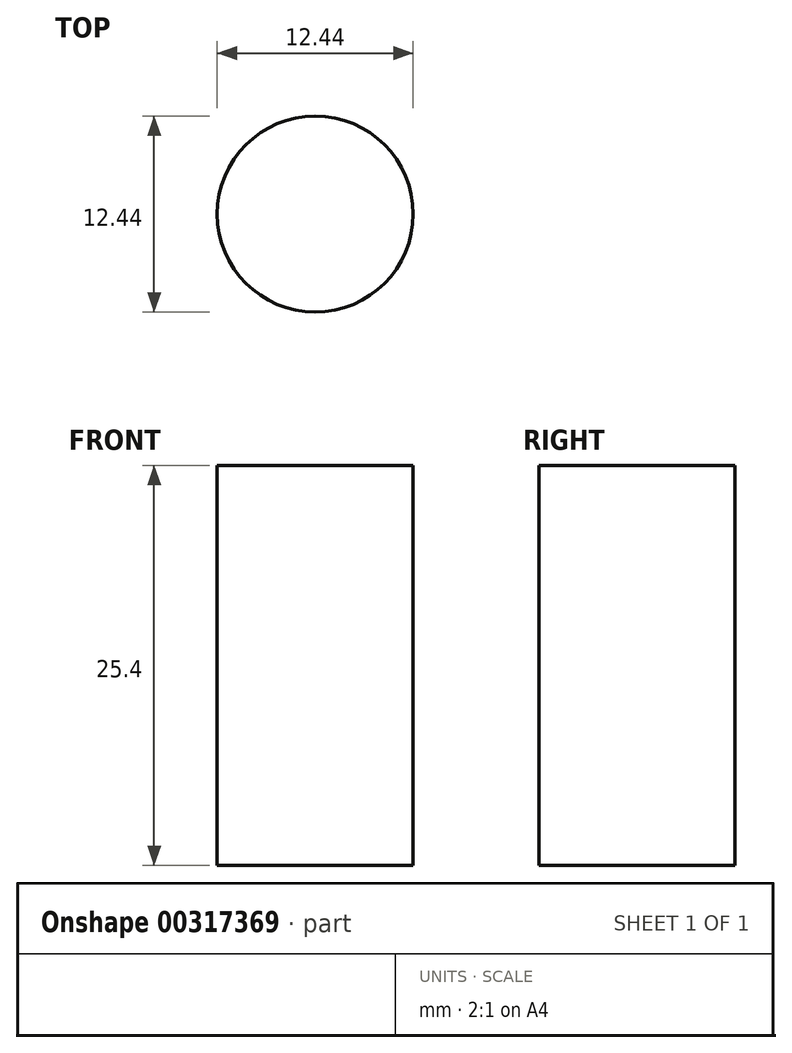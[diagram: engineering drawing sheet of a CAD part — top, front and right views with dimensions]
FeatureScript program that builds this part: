
annotation { "Feature Type Name" : "Feature", "Feature Type Description" : "" }
export const myFeature = defineFeature(function(context is Context, id is Id, definition is map)
    precondition{}
    {
        {
            var Q0;
            Q0=qCreatedBy(makeId("Top.planeOp"),FACE);
            var sketch = newSketch(context, id + "F0", { "sketchPlane" : qUnion([Q0])});
            skCircle(sketch, "E0", {"center": v(0, 0) * mm, "radius": 6.22 * mm});
            skSolve(sketch);
        }
        {
            var Q0;
            Q0=makeQuery(id+"F0.imprint","IMPRINT",FACE,{"disambiguationData":[TD([[makeQuery(id+"F0.imprint","IMPRINT",EDGE,{"derivedFrom":sQuery(id+"F0.wireOp",EDGE,"E0")}),1.0]])]});
            extrude(context, id + "F1", {"entities" : qUnion([Q0]), "depth" : 25.4 * mm});
        }
    });
